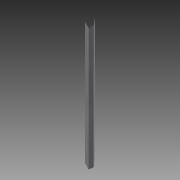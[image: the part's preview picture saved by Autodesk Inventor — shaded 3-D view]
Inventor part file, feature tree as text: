
AUTODESK INVENTOR PART (.ipt)
format: ipt  version: 2014 (Build 180170000, 170)  size: 73,216 bytes
history: native  units: in
note: dims shown in document units (in); Inventor stores cm internally (conversion verified against a paired STEP export)
features: extrude x1, sketch x1
ambient origin geometry x8: Origin, YZ Plane, XZ Plane, XY Plane, X Axis, Y Axis, Z Axis, Center Point
bodies: Solid1 (feature_tree)
feature tree (2):
  extrude  "Extrusion1"  Depth=10.5in TaperAngle=0.0deg
  sketch  "Sketch1"  dims[d0=0.5in d1=10.5in d2=0.0in]
